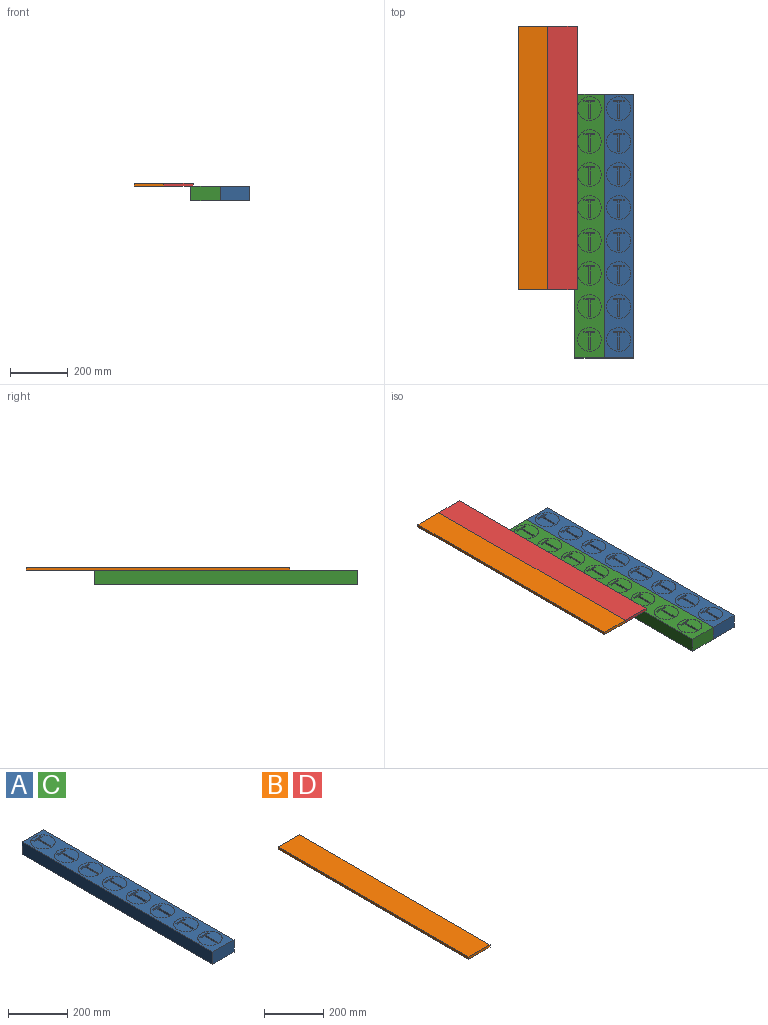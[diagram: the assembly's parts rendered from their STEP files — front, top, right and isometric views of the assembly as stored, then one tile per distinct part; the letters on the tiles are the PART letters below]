
ASSEMBLY  parts=4 mates=3
PART A: 94 faces, bbox 101.6x914.4x50.8 mm
  f0: plane 82.55x82.55mm, normal (0,0,1), area 4743.1mm2, adj f21,f85,f86,f87,f88,f89,f90,f91
  f1: plane 82.55x82.55mm, normal (0,0,1), area 4743.1mm2, adj f20,f76,f77,f78,f79,f80,f81,f82
  f2: plane 82.55x82.55mm, normal (0,0,1), area 4743.1mm2, adj f19,f67,f68,f69,f70,f71,f72,f73
  f3: plane 82.55x82.55mm, normal (0,0,1), area 4743.1mm2, adj f18,f58,f59,f60,f61,f62,f63,f64
  f4: plane 82.55x82.55mm, normal (0,0,1), area 4743.1mm2, adj f17,f49,f50,f51,f52,f53,f54,f55
  f5: plane 82.55x82.55mm, normal (0,0,1), area 4743.1mm2, adj f16,f40,f41,f42,f43,f44,f45,f46
  f6: plane 82.55x82.55mm, normal (0,0,1), area 4743.1mm2, adj f15,f31,f32,f33,f34,f35,f36,f37
  f7: plane 82.55x82.55mm, normal (0,0,1), area 4743.1mm2, adj f14,f22,f23,f24,f25,f26,f27,f28
  f8: plane 101.6x50.8mm, normal (0,1,0), area 5161.3mm2, adj f9,f11,f12,f13
  f9: plane 914.4x50.8mm, normal (-1,0,0), area 46451.5mm2, adj f8,f10,f12,f13
  f10: plane 101.6x50.8mm, normal (0,-1,0), area 5161.3mm2, adj f9,f11,f12,f13
  f11: plane 914.4x50.8mm, normal (1,0,0), area 46451.5mm2, adj f8,f10,f12,f13
  f12: plane 914.4x101.6mm, normal (0,0,1), area 50086.3mm2, adj f8,f9,f10,f11,f14,f15,f16,f17
  f13: plane 914.4x101.6mm, normal (0,0,-1), area 92903mm2, adj f8,f9,f10,f11
  f14: cylinder r=41.27mm len=82.55mm, axis (0,0,1), area 65.9mm2, adj f7,f12
  f15: cylinder r=41.27mm len=82.55mm, axis (0,0,1), area 65.9mm2, adj f6,f12
  f16: cylinder r=41.27mm len=82.55mm, axis (0,0,1), area 65.9mm2, adj f5,f12
  f17: cylinder r=41.27mm len=82.55mm, axis (0,0,1), area 65.9mm2, adj f4,f12
  f18: cylinder r=41.27mm len=82.55mm, axis (0,0,1), area 65.9mm2, adj f3,f12
  f19: cylinder r=41.27mm len=82.55mm, axis (0,0,1), area 65.9mm2, adj f2,f12
  f20: cylinder r=41.27mm len=82.55mm, axis (0,0,1), area 65.9mm2, adj f1,f12
  f21: cylinder r=41.27mm len=82.55mm, axis (0,0,1), area 65.9mm2, adj f0,f12
  f22: plane 50.29x38.1mm, normal (0,-1,0), area 1916.1mm2, adj f7,f23,f29,f30
  f23: plane 50.29x6.35mm, normal (1,0,0), area 319.4mm2, adj f7,f22,f24,f30
  f24: plane 50.29x15.88mm, normal (0,1,0), area 798.4mm2, adj f7,f23,f25,f30
  f25: plane 57.7x50.29mm, normal (1,0,0), area 2902mm2, adj f7,f24,f26,f30
  f26: cylinder r=34.92mm len=50.29mm, axis (0,0,1), area 319.8mm2, adj f7,f25,f27,f30
  f27: plane 57.7x50.29mm, normal (-1,0,0), area 2902mm2, adj f7,f26,f28,f30
  f28: plane 50.29x15.88mm, normal (0,1,0), area 798.4mm2, adj f7,f27,f29,f30
  f29: plane 50.29x6.35mm, normal (-1,0,0), area 319.4mm2, adj f7,f22,f28,f30
  f30: plane 64.2x38.1mm, normal (0,0,1), area 609mm2, adj f22,f23,f24,f25,f26,f27,f28,f29
  f31: plane 50.29x38.1mm, normal (0,-1,0), area 1916.1mm2, adj f6,f32,f38,f39
  f32: plane 50.29x6.35mm, normal (1,0,0), area 319.4mm2, adj f6,f31,f33,f39
  f33: plane 50.29x15.88mm, normal (0,1,0), area 798.4mm2, adj f6,f32,f34,f39
  f34: plane 57.7x50.29mm, normal (1,0,0), area 2902mm2, adj f6,f33,f35,f39
  f35: cylinder r=34.92mm len=50.29mm, axis (0,0,1), area 319.8mm2, adj f6,f34,f36,f39
  f36: plane 57.7x50.29mm, normal (-1,0,0), area 2902mm2, adj f6,f35,f37,f39
  f37: plane 50.29x15.88mm, normal (0,1,0), area 798.4mm2, adj f6,f36,f38,f39
  f38: plane 50.29x6.35mm, normal (-1,0,0), area 319.4mm2, adj f6,f31,f37,f39
  f39: plane 64.2x38.1mm, normal (0,0,1), area 609mm2, adj f31,f32,f33,f34,f35,f36,f37,f38
  f40: plane 50.29x38.1mm, normal (0,-1,0), area 1916.1mm2, adj f5,f41,f47,f48
  f41: plane 50.29x6.35mm, normal (1,0,0), area 319.4mm2, adj f5,f40,f42,f48
  f42: plane 50.29x15.88mm, normal (0,1,0), area 798.4mm2, adj f5,f41,f43,f48
  f43: plane 57.7x50.29mm, normal (1,0,0), area 2902mm2, adj f5,f42,f44,f48
  f44: cylinder r=34.92mm len=50.29mm, axis (0,0,1), area 319.8mm2, adj f5,f43,f45,f48
  f45: plane 57.7x50.29mm, normal (-1,0,0), area 2902mm2, adj f5,f44,f46,f48
  f46: plane 50.29x15.88mm, normal (0,1,0), area 798.4mm2, adj f5,f45,f47,f48
  f47: plane 50.29x6.35mm, normal (-1,0,0), area 319.4mm2, adj f5,f40,f46,f48
  f48: plane 64.2x38.1mm, normal (0,0,1), area 609mm2, adj f40,f41,f42,f43,f44,f45,f46,f47
  f49: plane 50.29x38.1mm, normal (0,-1,0), area 1916.1mm2, adj f4,f50,f56,f57
  f50: plane 50.29x6.35mm, normal (1,0,0), area 319.4mm2, adj f4,f49,f51,f57
  f51: plane 50.29x15.88mm, normal (0,1,0), area 798.4mm2, adj f4,f50,f52,f57
  f52: plane 57.7x50.29mm, normal (1,0,0), area 2902mm2, adj f4,f51,f53,f57
  f53: cylinder r=34.92mm len=50.29mm, axis (0,0,1), area 319.8mm2, adj f4,f52,f54,f57
  f54: plane 57.7x50.29mm, normal (-1,0,0), area 2902mm2, adj f4,f53,f55,f57
  f55: plane 50.29x15.88mm, normal (0,1,0), area 798.4mm2, adj f4,f54,f56,f57
  f56: plane 50.29x6.35mm, normal (-1,0,0), area 319.4mm2, adj f4,f49,f55,f57
  f57: plane 64.2x38.1mm, normal (0,0,1), area 609mm2, adj f49,f50,f51,f52,f53,f54,f55,f56
  f58: plane 50.29x38.1mm, normal (0,-1,0), area 1916.1mm2, adj f3,f59,f65,f66
  f59: plane 50.29x6.35mm, normal (1,0,0), area 319.4mm2, adj f3,f58,f60,f66
  f60: plane 50.29x15.88mm, normal (0,1,0), area 798.4mm2, adj f3,f59,f61,f66
  f61: plane 57.7x50.29mm, normal (1,0,0), area 2902mm2, adj f3,f60,f62,f66
  f62: cylinder r=34.92mm len=50.29mm, axis (0,0,1), area 319.8mm2, adj f3,f61,f63,f66
  f63: plane 57.7x50.29mm, normal (-1,0,0), area 2902mm2, adj f3,f62,f64,f66
  f64: plane 50.29x15.88mm, normal (0,1,0), area 798.4mm2, adj f3,f63,f65,f66
  f65: plane 50.29x6.35mm, normal (-1,0,0), area 319.4mm2, adj f3,f58,f64,f66
  f66: plane 64.2x38.1mm, normal (0,0,1), area 609mm2, adj f58,f59,f60,f61,f62,f63,f64,f65
  f67: plane 50.29x38.1mm, normal (0,-1,0), area 1916.1mm2, adj f2,f68,f74,f75
  f68: plane 50.29x6.35mm, normal (1,0,0), area 319.4mm2, adj f2,f67,f69,f75
  f69: plane 50.29x15.88mm, normal (0,1,0), area 798.4mm2, adj f2,f68,f70,f75
  f70: plane 57.7x50.29mm, normal (1,0,0), area 2902mm2, adj f2,f69,f71,f75
  f71: cylinder r=34.92mm len=50.29mm, axis (0,0,1), area 319.8mm2, adj f2,f70,f72,f75
  f72: plane 57.7x50.29mm, normal (-1,0,0), area 2902mm2, adj f2,f71,f73,f75
  f73: plane 50.29x15.88mm, normal (0,1,0), area 798.4mm2, adj f2,f72,f74,f75
  f74: plane 50.29x6.35mm, normal (-1,0,0), area 319.4mm2, adj f2,f67,f73,f75
  f75: plane 64.2x38.1mm, normal (0,0,1), area 609mm2, adj f67,f68,f69,f70,f71,f72,f73,f74
  f76: plane 50.29x38.1mm, normal (0,-1,0), area 1916.1mm2, adj f1,f77,f83,f84
  f77: plane 50.29x6.35mm, normal (1,0,0), area 319.4mm2, adj f1,f76,f78,f84
  f78: plane 50.29x15.88mm, normal (0,1,0), area 798.4mm2, adj f1,f77,f79,f84
  f79: plane 57.7x50.29mm, normal (1,0,0), area 2902mm2, adj f1,f78,f80,f84
  f80: cylinder r=34.92mm len=50.29mm, axis (0,0,1), area 319.8mm2, adj f1,f79,f81,f84
  f81: plane 57.7x50.29mm, normal (-1,0,0), area 2902mm2, adj f1,f80,f82,f84
  f82: plane 50.29x15.88mm, normal (0,1,0), area 798.4mm2, adj f1,f81,f83,f84
  f83: plane 50.29x6.35mm, normal (-1,0,0), area 319.4mm2, adj f1,f76,f82,f84
  f84: plane 64.2x38.1mm, normal (0,0,1), area 609mm2, adj f76,f77,f78,f79,f80,f81,f82,f83
  f85: plane 50.29x38.1mm, normal (0,-1,0), area 1916.1mm2, adj f0,f86,f92,f93
  f86: plane 50.29x6.35mm, normal (1,0,0), area 319.4mm2, adj f0,f85,f87,f93
  f87: plane 50.29x15.88mm, normal (0,1,0), area 798.4mm2, adj f0,f86,f88,f93
  f88: plane 57.7x50.29mm, normal (1,0,0), area 2902mm2, adj f0,f87,f89,f93
  f89: cylinder r=34.92mm len=50.29mm, axis (0,0,1), area 319.8mm2, adj f0,f88,f90,f93
  f90: plane 57.7x50.29mm, normal (-1,0,0), area 2902mm2, adj f0,f89,f91,f93
  f91: plane 50.29x15.88mm, normal (0,1,0), area 798.4mm2, adj f0,f90,f92,f93
  f92: plane 50.29x6.35mm, normal (-1,0,0), area 319.4mm2, adj f0,f85,f91,f93
  f93: plane 64.2x38.1mm, normal (0,0,1), area 609mm2, adj f85,f86,f87,f88,f89,f90,f91,f92
PART B: 6 faces, bbox 101.6x914.4x9.5 mm
  f0: plane 101.6x9.53mm, normal (0,1,0), area 967.7mm2, adj f1,f3,f4,f5
  f1: plane 914.4x9.53mm, normal (-1,0,0), area 8709.7mm2, adj f0,f2,f4,f5
  f2: plane 101.6x9.53mm, normal (0,-1,0), area 967.7mm2, adj f1,f3,f4,f5
  f3: plane 914.4x9.53mm, normal (1,0,0), area 8709.7mm2, adj f0,f2,f4,f5
  f4: plane 914.4x101.6mm, normal (0,0,1), area 92903mm2, adj f0,f1,f2,f3
  f5: plane 914.4x101.6mm, normal (0,0,-1), area 92903mm2, adj f0,f1,f2,f3
PART C: same geometry as A
PART D: same geometry as B
PLACE A t=(-142.86,-199.45,196.23)mm
PLACE B t=(-439.97,36.41,247.03)mm
PLACE C t=(-244.46,-199.45,196.23)mm
PLACE D t=(-338.37,36.41,247.03)mm
MATE fastened B.f3 <-> D.f1  axis (1,0,0) through (-338.37,-420.79,251.8)mm
MATE planar A.f12 <-> D.f5  axis (0,0,1) through (-91.52,-662.64,247.03)mm
MATE fastened A.f9 <-> C.f11  axis (-1,0,0) through (-142.86,-656.65,221.63)mm
